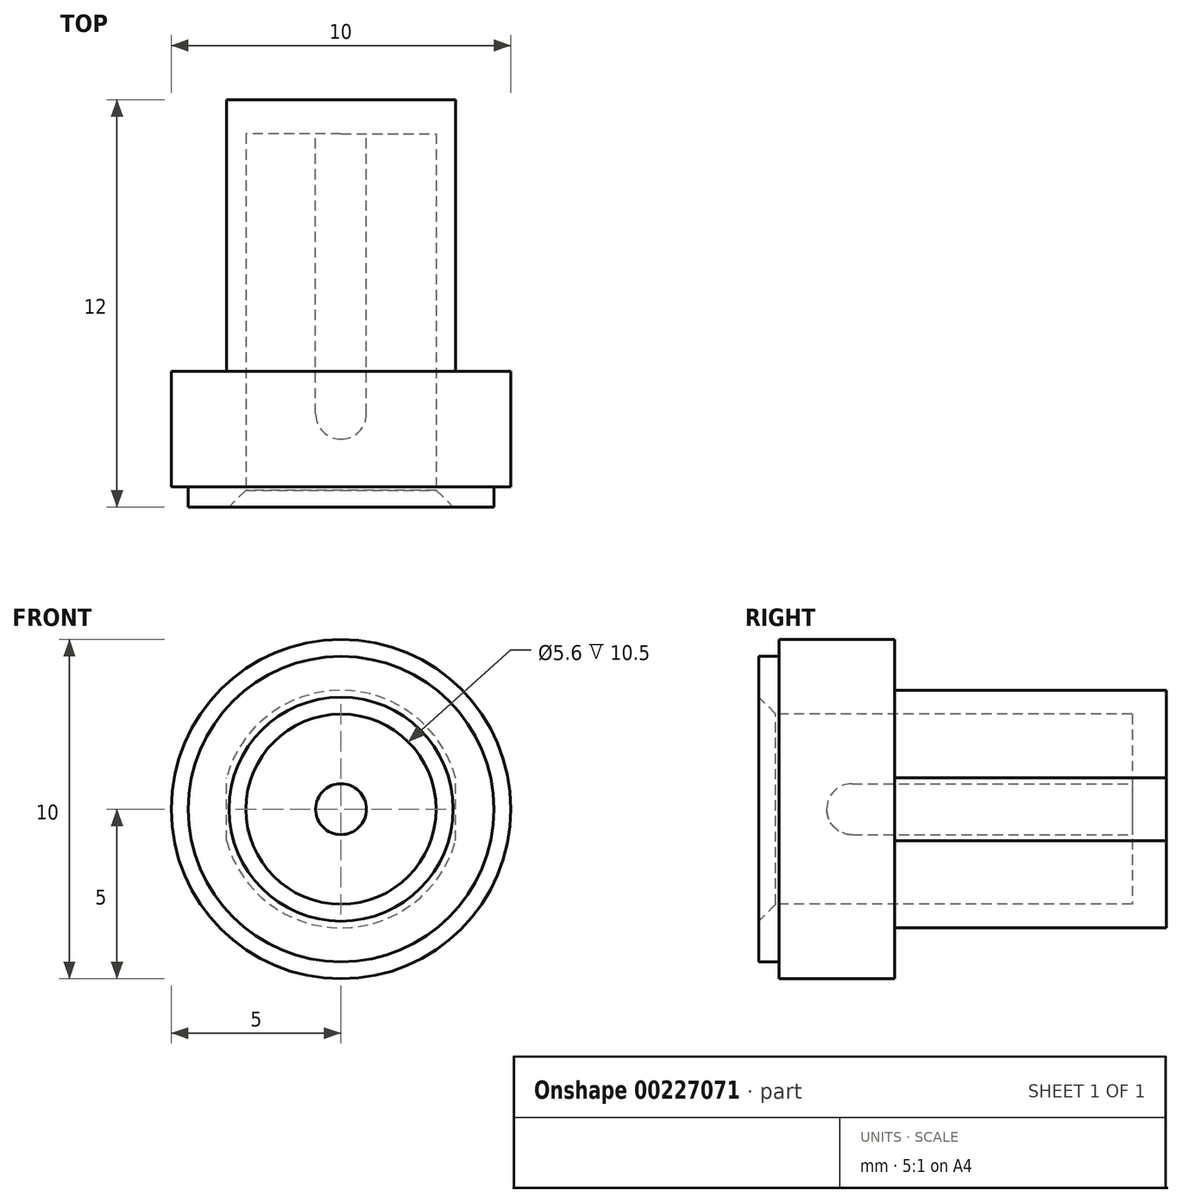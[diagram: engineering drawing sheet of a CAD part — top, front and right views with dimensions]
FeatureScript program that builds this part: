
annotation { "Feature Type Name" : "Feature", "Feature Type Description" : "" }
export const myFeature = defineFeature(function(context is Context, id is Id, definition is map)
    precondition{}
    {
        {
            var Q0;
            Q0=qCreatedBy(makeId("Front.planeOp"),FACE);
            var sketch = newSketch(context, id + "F0", { "sketchPlane" : qUnion([Q0])});
            skCircle(sketch, "E0", {"center": v(0, 0) * mm, "radius": 5 * mm});
            skSolve(sketch);
        }
        {
            var Q0;
            Q0=makeQuery(id+"F0.imprint","IMPRINT",FACE,{"disambiguationData":[TD([[makeQuery(id+"F0.imprint","IMPRINT",EDGE,{"derivedFrom":sQuery(id+"F0.wireOp",EDGE,"E0")}),1.0]])]});
            extrude(context, id + "F1", {"entities" : qUnion([Q0]), "depth" : 3.4 * mm, "offsetDistance" : 25 * mm});
        }
        {
            var Q0;
            Q0=makeQuery(id+"F1.opExtrude","CAP_FACE",FACE,{"disambiguationData":[OSD([sQuery(id+"F0.wireOp",EDGE,"E0")])],"isStart":true});
            var sketch = newSketch(context, id + "F2", { "sketchPlane" : qUnion([Q0])});
            skCircle(sketch, "E1", {"center": v(0, 0) * mm, "radius": 3.5 * mm});
            skSolve(sketch);
        }
        {
            var Q0;
            Q0=makeQuery(id+"F2.imprint","IMPRINT",FACE,{"disambiguationData":[TD([[makeQuery(id+"F2.imprint","IMPRINT",EDGE,{"derivedFrom":sQuery(id+"F2.wireOp",EDGE,"E1")}),1.0]])]});
            extrude(context, id + "F3", {"entities" : qUnion([Q0]), "operationType" : NewBodyOperationType.ADD, "depth" : 8 * mm, "offsetDistance" : 25 * mm});
        }
        {
            var Q0;
            Q0=makeQuery(id+"F3.opExtrude","CAP_FACE",FACE,{"disambiguationData":[OSD([sQuery(id+"F2.wireOp",EDGE,"E1")])],"isStart":false});
            var sketch = newSketch(context, id + "F4", { "sketchPlane" : qUnion([Q0])});
            skLineSegment(sketch, "E2.bottom", {"start": v(-3.38, -0.93) * mm, "end": v(3.38, -0.93) * mm});
            skLineSegment(sketch, "E2.top", {"start": v(-3.38, 0.93) * mm, "end": v(3.38, 0.93) * mm});
            skLineSegment(sketch, "E2.left", {"start": v(-3.38, -0.93) * mm, "end": v(-3.38, 0.93) * mm});
            skLineSegment(sketch, "E2.right", {"start": v(3.38, -0.93) * mm, "end": v(3.38, 0.93) * mm});
            skPoint(sketch, "E2.middle", {"position": v(0, 0) * mm});
            skSolve(sketch);
        }
        {
            var Q0;
            {var subQ0=sQuery(id+"F4.wireOp",EDGE,"E2.right");Q0=makeQuery(id+"F4.imprint","IMPRINT",FACE,{"disambiguationData":[TD([[makeQuery(id+"F4.imprint","IMPRINT",EDGE,{"derivedFrom":subQ0}),-1.0]])]});}
            var Q1;
            {var subQ0=sQuery(id+"F4.wireOp",EDGE,"E2.left");Q1=makeQuery(id+"F4.imprint","IMPRINT",FACE,{"disambiguationData":[TD([[makeQuery(id+"F4.imprint","IMPRINT",EDGE,{"derivedFrom":subQ0}),1.0]])]});}
            var Q2;
            Q2=makeQuery(id+"F1.opExtrude","CAP_FACE",FACE,{"disambiguationData":[OSD([sQuery(id+"F0.wireOp",EDGE,"E0")])],"isStart":true});
            extrude(context, id + "F5", {"entities" : qUnion([Q0, Q1]), "operationType" : NewBodyOperationType.REMOVE, "endBound" : BoundingType.UP_TO_SURFACE, "oppositeDirection" : true, "depth" : 25 * mm, "endBoundEntityFace" : qUnion([Q2]), "offsetDistance" : 25 * mm});
        }
        {
            var Q0;
            Q0=makeQuery(id+"F1.opExtrude","CAP_FACE",FACE,{"disambiguationData":[OSD([sQuery(id+"F0.wireOp",EDGE,"E0")])],"isStart":false});
            var sketch = newSketch(context, id + "F6", { "sketchPlane" : qUnion([Q0])});
            skCircle(sketch, "E3", {"center": v(0, 0) * mm, "radius": 3 * mm});
            skSolve(sketch);
        }
        {
            var Q0;
            Q0=makeQuery(id+"F6.imprint","IMPRINT",FACE,{"disambiguationData":[TD([[makeQuery(id+"F6.imprint","IMPRINT",EDGE,{"derivedFrom":sQuery(id+"F6.wireOp",EDGE,"E3")}),1.0]])]});
            var Q1;
            Q1=makeQuery(id+"F3.opExtrude","CAP_FACE",FACE,{"disambiguationData":[OSD([sQuery(id+"F2.wireOp",EDGE,"E1")])],"isStart":false});
            extrude(context, id + "F7", {"entities" : qUnion([Q0]), "operationType" : NewBodyOperationType.REMOVE, "endBound" : BoundingType.UP_TO_SURFACE, "oppositeDirection" : true, "depth" : 25 * mm, "endBoundEntityFace" : qUnion([Q1]), "hasOffset" : true, "offsetDistance" : 1 * mm});
        }
        {
            var Q0;
            Q0=makeQuery(id+"F1.opExtrude","CAP_FACE",FACE,{"disambiguationData":[OSD([sQuery(id+"F0.wireOp",EDGE,"E0")])],"isStart":false});
            var sketch = newSketch(context, id + "F8", { "sketchPlane" : qUnion([Q0])});
            skCircle(sketch, "E4", {"center": v(0, 0) * mm, "radius": 2.8 * mm});
            skSolve(sketch);
        }
        {
            var Q0;
            Q0=makeQuery(id+"F8.imprint","IMPRINT",FACE,{"disambiguationData":[TD([[makeQuery(id+"F8.imprint","IMPRINT",EDGE,{"derivedFrom":sQuery(id+"F8.wireOp",EDGE,"E4")}),-1.0]])]});
            var Q1;
            Q1=makeQuery(id+"F7.boolean.opBoolean","COPY",FACE,{"derivedFrom":makeQuery(id+"F7.opExtrude","CAP_FACE",FACE,{"disambiguationData":[OSD([sQuery(id+"F6.wireOp",EDGE,"E3")])],"isStart":false})});
            extrude(context, id + "F9", {"entities" : qUnion([Q0]), "endBound" : BoundingType.UP_TO_SURFACE, "oppositeDirection" : true, "depth" : 25 * mm, "endBoundEntityFace" : qUnion([Q1]), "offsetDistance" : 25 * mm});
        }
        {
            var Q0;
            Q0=makeQuery(id+"F9.opExtrude","CAP_FACE",FACE,{"disambiguationData":[OSD([sQuery(id+"F6.wireOp",EDGE,"E3"),sQuery(id+"F8.wireOp",EDGE,"E4")])],"isStart":true});
            var sketch = newSketch(context, id + "F10", { "sketchPlane" : qUnion([Q0])});
            skCircle(sketch, "E5", {"center": v(0, 0) * mm, "radius": 4.5 * mm});
            skSolve(sketch);
        }
        {
            var Q0;
            Q0=makeQuery(id+"F10.imprint","IMPRINT",FACE,{"disambiguationData":[TD([[makeQuery(id+"F10.imprint","IMPRINT",EDGE,{"derivedFrom":sQuery(id+"F10.wireOp",EDGE,"E5")}),1.0]])]});
            var Q1;
            Q1=makeQuery(id+"F10.imprint","IMPRINT",FACE,{"disambiguationData":[TD([[makeQuery(id+"F10.imprint","IMPRINT",EDGE,{"derivedFrom":makeQuery(id+"F9.opExtrude","CAP_EDGE",EDGE,{"disambiguationData":[OSD([sQuery(id+"F8.wireOp",EDGE,"E4")])],"isStart":true})}),-1.0]])]});
            extrude(context, id + "F11", {"entities" : qUnion([Q0, Q1]), "operationType" : NewBodyOperationType.ADD, "depth" : 0.6 * mm, "offsetDistance" : 25 * mm});
        }
        {
            var Q0;
            Q0=makeQuery(id+"F11.opExtrude","CAP_EDGE",EDGE,{"disambiguationData":[OSD([sQuery(id+"F8.wireOp",EDGE,"E4")])],"isStart":false});
            chamfer(context, id + "F12", {"entities" : qUnion([Q0]), "width" : .5 * mm, "tangentPropagation" : true});
        }
        {
            var Q0;
            Q0=makeQuery(id+"F7.boolean.opBoolean","COPY",FACE,{"derivedFrom":makeQuery(id+"F7.opExtrude","CAP_FACE",FACE,{"disambiguationData":[OSD([sQuery(id+"F6.wireOp",EDGE,"E3")])],"isStart":false})});
            var sketch = newSketch(context, id + "F13", { "sketchPlane" : qUnion([Q0])});
            skCircle(sketch, "E6", {"center": v(0, 0) * mm, "radius": 0.75 * mm});
            skSolve(sketch);
        }
        {
            var Q0;
            Q0=makeQuery(id+"F13.imprint","IMPRINT",FACE,{"disambiguationData":[TD([[makeQuery(id+"F13.imprint","IMPRINT",EDGE,{"derivedFrom":sQuery(id+"F13.wireOp",EDGE,"E6")}),1.0]])]});
            extrude(context, id + "F14", {"entities" : qUnion([Q0]), "depth" : 9 * mm, "offsetDistance" : 25 * mm});
        }
        {
            var Q0;
            Q0=makeQuery(id+"F14.opExtrude","CAP_EDGE",EDGE,{"disambiguationData":[OSD([sQuery(id+"F13.wireOp",EDGE,"E6")])],"isStart":false});
            fillet(context, id + "F15", {"entities" : qUnion([Q0]), "radius" : 0.75 * mm, "tangentPropagation" : true, "allowEdgeOverflow" : false});
        }
    });
